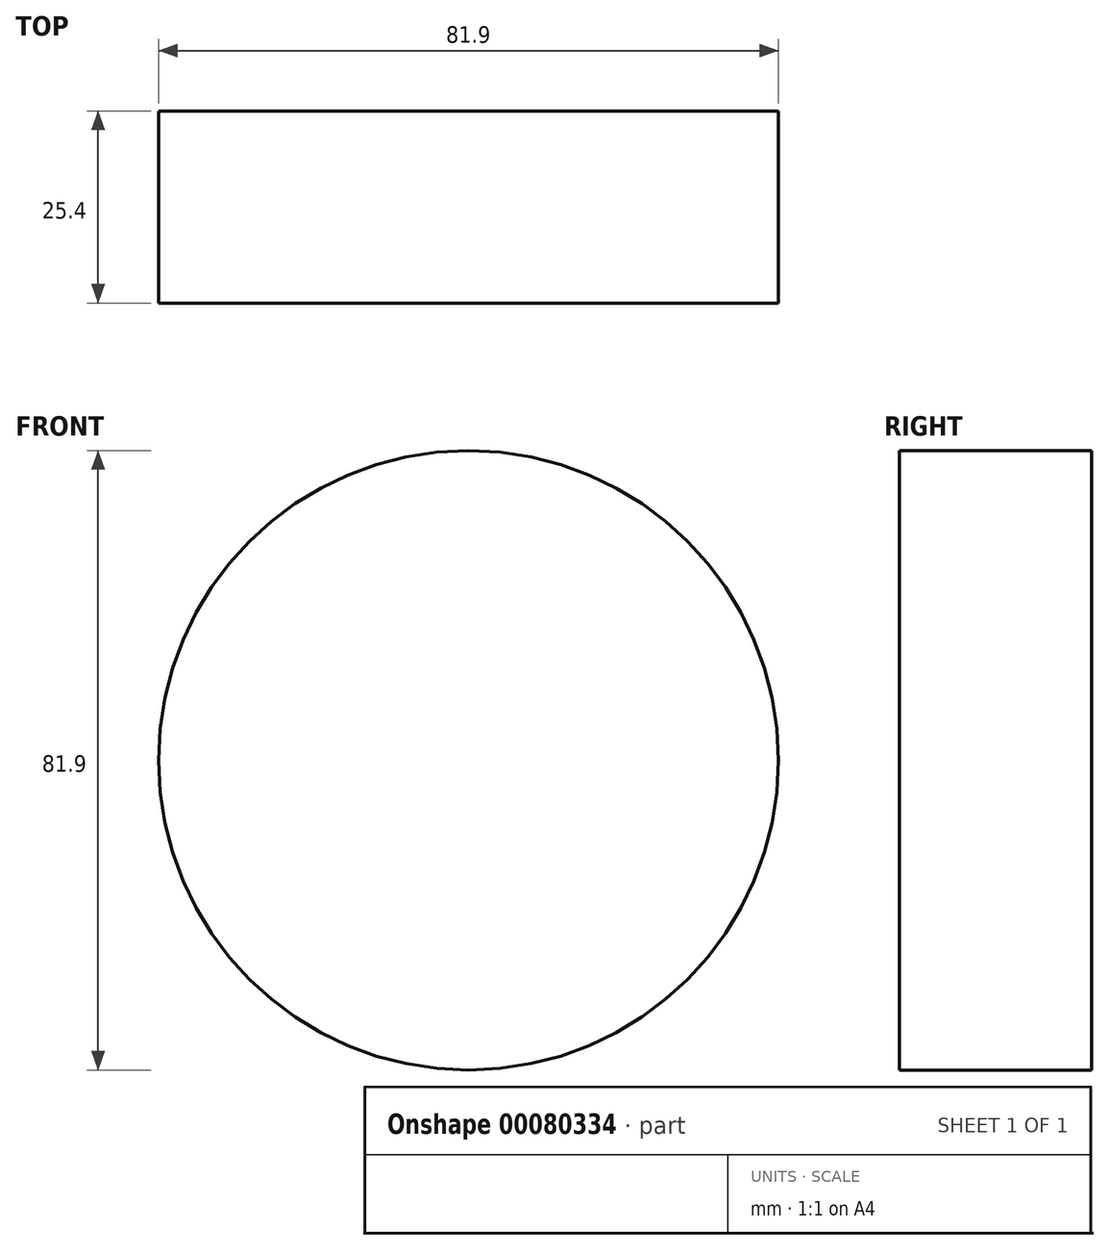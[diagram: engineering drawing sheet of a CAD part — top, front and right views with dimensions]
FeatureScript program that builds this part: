
annotation { "Feature Type Name" : "Feature", "Feature Type Description" : "" }
export const myFeature = defineFeature(function(context is Context, id is Id, definition is map)
    precondition{}
    {
        {
            var Q0;
            Q0=qCreatedBy(makeId("Front.planeOp"),FACE);
            var sketch = newSketch(context, id + "F0", { "sketchPlane" : qUnion([Q0])});
            skCircle(sketch, "E0", {"center": v(0, 0) * mm, "radius": 40.95 * mm});
            skSolve(sketch);
        }
        {
            var Q0;
            Q0=makeQuery(id+"F0.imprint","IMPRINT",FACE,{"disambiguationData":[TD([[makeQuery(id+"F0.imprint","IMPRINT",EDGE,{"derivedFrom":sQuery(id+"F0.wireOp",EDGE,"E0")}),1.0]])]});
            extrude(context, id + "F1", {"entities" : qUnion([Q0]), "depth" : 25.4 * mm});
        }
    });
